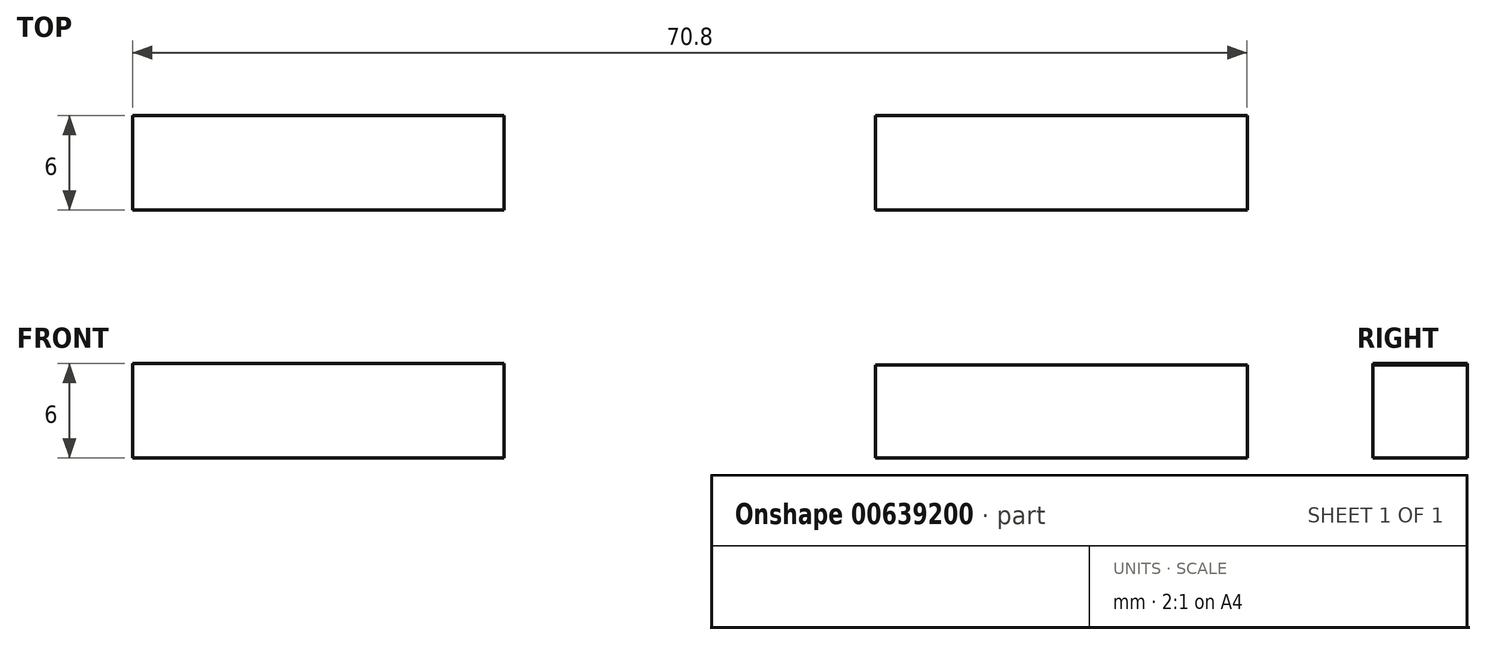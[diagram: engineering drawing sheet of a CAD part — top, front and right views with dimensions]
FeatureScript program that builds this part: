
annotation { "Feature Type Name" : "Feature", "Feature Type Description" : "" }
export const myFeature = defineFeature(function(context is Context, id is Id, definition is map)
    precondition{}
    {
        {
            var Q0;
            Q0=qCreatedBy(makeId("Front.planeOp"),FACE);
            var sketch = newSketch(context, id + "F0", { "sketchPlane" : qUnion([Q0])});
            skLineSegment(sketch, "E0.bottom", {"start": v(-58, 43.56) * mm, "end": v(60, 43.56) * mm});
            skLineSegment(sketch, "E0.top", {"start": v(-58, -26.44) * mm, "end": v(60, -26.44) * mm});
            skLineSegment(sketch, "E1.bottom", {"start": v(-58, 43.56) * mm, "end": v(-34.4, 43.56) * mm});
            skLineSegment(sketch, "E1.top", {"start": v(-58, 37.56) * mm, "end": v(-34.4, 37.56) * mm});
            skLineSegment(sketch, "E1.left", {"start": v(-58, 43.56) * mm, "end": v(-58, 37.56) * mm});
            skLineSegment(sketch, "E1.right", {"start": v(-34.4, 43.56) * mm, "end": v(-34.4, 37.56) * mm});
            skLineSegment(sketch, "E2.1.0.0", {"start": v(-10.8, 43.56) * mm, "end": v(-10.8, 37.56) * mm});
            skLineSegment(sketch, "E2.2.0.0", {"start": v(12.8, 43.56) * mm, "end": v(12.8, 37.56) * mm});
            skLineSegment(sketch, "E2.2.0.1", {"start": v(-10.8, 37.56) * mm, "end": v(12.8, 37.56) * mm});
            skLineSegment(sketch, "E2.3.0.0", {"start": v(36.4, 43.56) * mm, "end": v(36.4, 37.56) * mm});
            skLineSegment(sketch, "E2.3.0.1", {"start": v(12.8, 37.56) * mm, "end": v(36.4, 37.56) * mm});
            skLineSegment(sketch, "E2.4.0.1", {"start": v(37.32, 37.46) * mm, "end": v(60.92, 37.46) * mm});
            skLineSegment(sketch, "E3.MirrorCS", {"start": v(-58.47, -20.44) * mm, "end": v(-34.87, -20.44) * mm});
            skLineSegment(sketch, "E4.MirrorCS", {"start": v(-34.4, -26.44) * mm, "end": v(-34.4, -20.44) * mm});
            skLineSegment(sketch, "E5.MirrorCS", {"start": v(-58, -26.44) * mm, "end": v(-34.4, -26.44) * mm});
            skLineSegment(sketch, "E6.MirrorCS", {"start": v(-10.8, -26.44) * mm, "end": v(-10.8, -20.44) * mm});
            skLineSegment(sketch, "E7.MirrorCS", {"start": v(-10.8, -20.44) * mm, "end": v(12.8, -20.44) * mm});
            skLineSegment(sketch, "E8.MirrorCS", {"start": v(12.8, -26.44) * mm, "end": v(12.8, -20.44) * mm});
            skLineSegment(sketch, "E9.MirrorCS", {"start": v(36.4, -26.44) * mm, "end": v(36.4, -20.44) * mm});
            skLineSegment(sketch, "E10.MirrorCS", {"start": v(36.4, -20.54) * mm, "end": v(60, -20.54) * mm});
            skLineSegment(sketch, "E11.MirrorCS", {"start": v(36.4, -20.44) * mm, "end": v(60, -20.44) * mm});
            skLineSegment(sketch, "E12", {"start": v(-34.4, 37.56) * mm, "end": v(-10.8, 37.56) * mm});
            skLineSegment(sketch, "E13.bottom", {"start": v(-58, 37.56) * mm, "end": v(-52, 37.56) * mm});
            skLineSegment(sketch, "E14", {"start": v(-58, 18.26) * mm, "end": v(-52, 18.26) * mm});
            skLineSegment(sketch, "E15", {"start": v(-58, -1.14) * mm, "end": v(-52, -1.14) * mm});
            skLineSegment(sketch, "E16", {"start": v(-52, 18.26) * mm, "end": v(-52, -1.14) * mm});
            skLineSegment(sketch, "E17", {"start": v(-52, -1.14) * mm, "end": v(-52, -20.44) * mm});
            skLineSegment(sketch, "E18", {"start": v(-52, 18.26) * mm, "end": v(-52, 37.56) * mm});
            skLineSegment(sketch, "E19", {"start": v(-58, -1.14) * mm, "end": v(-58, 18.26) * mm});
            skLineSegment(sketch, "E20", {"start": v(60, 18.26) * mm, "end": v(60, -1.14) * mm});
            skLineSegment(sketch, "E21", {"start": v(60, 18.26) * mm, "end": v(54, 18.26) * mm});
            skLineSegment(sketch, "E22", {"start": v(54, 37.46) * mm, "end": v(54, 18.26) * mm});
            skLineSegment(sketch, "E23", {"start": v(60, -1.14) * mm, "end": v(54, -1.14) * mm});
            skLineSegment(sketch, "E24", {"start": v(54, -20.44) * mm, "end": v(54, -1.14) * mm});
            skLineSegment(sketch, "E25", {"start": v(60, 43.56) * mm, "end": v(60, 37.46) * mm});
            skPoint(sketch, "E25.endSnap0", {"position": v(49.12, 37.46) * mm});
            skLineSegment(sketch, "E26", {"start": v(60, -20.44) * mm, "end": v(60, -26.44) * mm});
            skLineSegment(sketch, "E27", {"start": v(-58.47, -20.44) * mm, "end": v(-58.47, -26.44) * mm});
            skSolve(sketch);
        }
        {
            var Q0;
            Q0=makeQuery(id+"F0.imprint","IMPRINT",FACE,{"disambiguationData":[TD([[makeQuery(id+"F0.imprint","IMPRINT",EDGE,{"derivedFrom":sQuery(id+"F0.wireOp",EDGE,"E1.bottom")}),-1.0]])]});
            var Q1;
            Q1=makeQuery(id+"F0.imprint","IMPRINT",FACE,{"disambiguationData":[TD([[makeQuery(id+"F0.imprint","IMPRINT",EDGE,{"derivedFrom":sQuery(id+"F0.wireOp",EDGE,"E0.top")}),1.0]])]});
            var Q2;
            {var subQ0=sQuery(id+"F0.wireOp",EDGE,"E2.1.0.0");Q2=makeQuery(id+"F0.imprint","IMPRINT",FACE,{"disambiguationData":[TD([[makeQuery(id+"F0.imprint","IMPRINT",EDGE,{"derivedFrom":subQ0}),1.0]])]});}
            var Q3;
            {var subQ2=sQuery(id+"F0.wireOp",EDGE,"E2.3.0.0");Q3=makeQuery(id+"F0.imprint","IMPRINT",FACE,{"disambiguationData":[TD([[makeQuery(id+"F0.imprint","IMPRINT",EDGE,{"derivedFrom":subQ2}),1.0]])]});}
            extrude(context, id + "F1", {"entities" : qUnion([Q0, Q1, Q2, Q3]), "depth" : 6 * mm, "offsetDistance" : 25 * mm});
        }
    });
